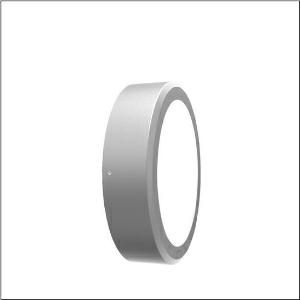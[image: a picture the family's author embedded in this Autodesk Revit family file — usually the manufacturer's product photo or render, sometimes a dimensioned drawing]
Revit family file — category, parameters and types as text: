
# Revit family: cl_31_bulkhead_5cl721603
name_source: partatom
category: Lighting Fixtures
units: mm (PartAtom-declared; Revit-internal decimal feet)

## family parameters
Cut with Voids When Loaded = No
Host = Face
Light Source = No
Part Type = Normal
Room Calculation Point = No
Round Connector Dimension = Use Diameter
Shared = No

## types (1)
- --- (1 x LED, 1570 lm, 14.9 W, 3000K)
    Apparent Load = 15 VA
    CIE Flux Codes = 46 78 95 100 100
    Color Rendering = 80
    Color Temperature = 3000K
    Default Elevation = 1800 mm
    Description = CL 31 Bulkhead, wall and ceiling luminaire, primary light control with reflector, primary optical cover: cover panel, of PC, opal, primary light characteristic: symmetric, installation type: surface-mounted, LED, rated luminous flux: 1.575lm, luminous efficacy: 105lm/W, light colour: 830, colour temperature: 3000K, control gear: DALI, with terminal, 5-pole, max. 2.5mm², mains connection: 220..240V, AC, 50/60Hz, rated input power: 15W, luminaire housing, round, of aluminium, powder-coated, SITECO metallic grey, diameter: 264mm, height: 63mm, protection rating (complete): IP65, insulation class (complete): insulation class I (protective earthing), certification: CE, ENEC, impact resistance: IK09, permissible operating ambient temperature for outdoor applications: -20..+50°C, packaging unit: 1 piece
    Height = 63 mm
    Lamp = 1 x LED
    Lamp Light Flux = 1570 lm
    Lamp Power = 14.9 W
    Lamp count = 1
    Length = 264 mm
    Luminous efficacy = 105 lm/W
    Manufacturer = Siteco
    ModVariant = No
    Model = 5CL721603
    Mounting Place = Wall
    Mounting Type = Surface mounted
    Number of Poles = 1
    OnlyDefault = Yes
    Power Factor = 1
    Product Name = CL 31 Bulkhead
    Product group = wall and ceiling luminaire | wall mounted
    ProductGroupID = 2001
    Protection Class = Protection class I
    Protection Degree = IP 65
    RLX_Detail_Level = 1
    RLX_Emergency_Light_Flux = 0 lm
    RLX_Emergency_Type = 0
    RLX_Emergency_Type_DB = No
    RlxData = <blob elided: 36869 chars, md5=8e752720>
    Socket = socket
    Standby Power = 0 W
    System Light Flux = 1570 lm
    System Power = 15 W
    Type Comments = factory setting: luminous flux: 100 % | dim-lin: 254 | 347 mA
    Type Image = l_1006885.jpg
    URL = http://relux.com
    VarID = @adj_194405
    Voltage = 0 V
    Weight = 0.00 kg
    Width = 0 mm  [stored 0 ft]

note: [stored X ft] marks values corroborated as IEEE doubles in the binary element streams (Revit-internal decimal feet)

## geometry (parser evidence)
native form markers: Blend x4, Sweep x9
no freeform markers — native parametric forms only
